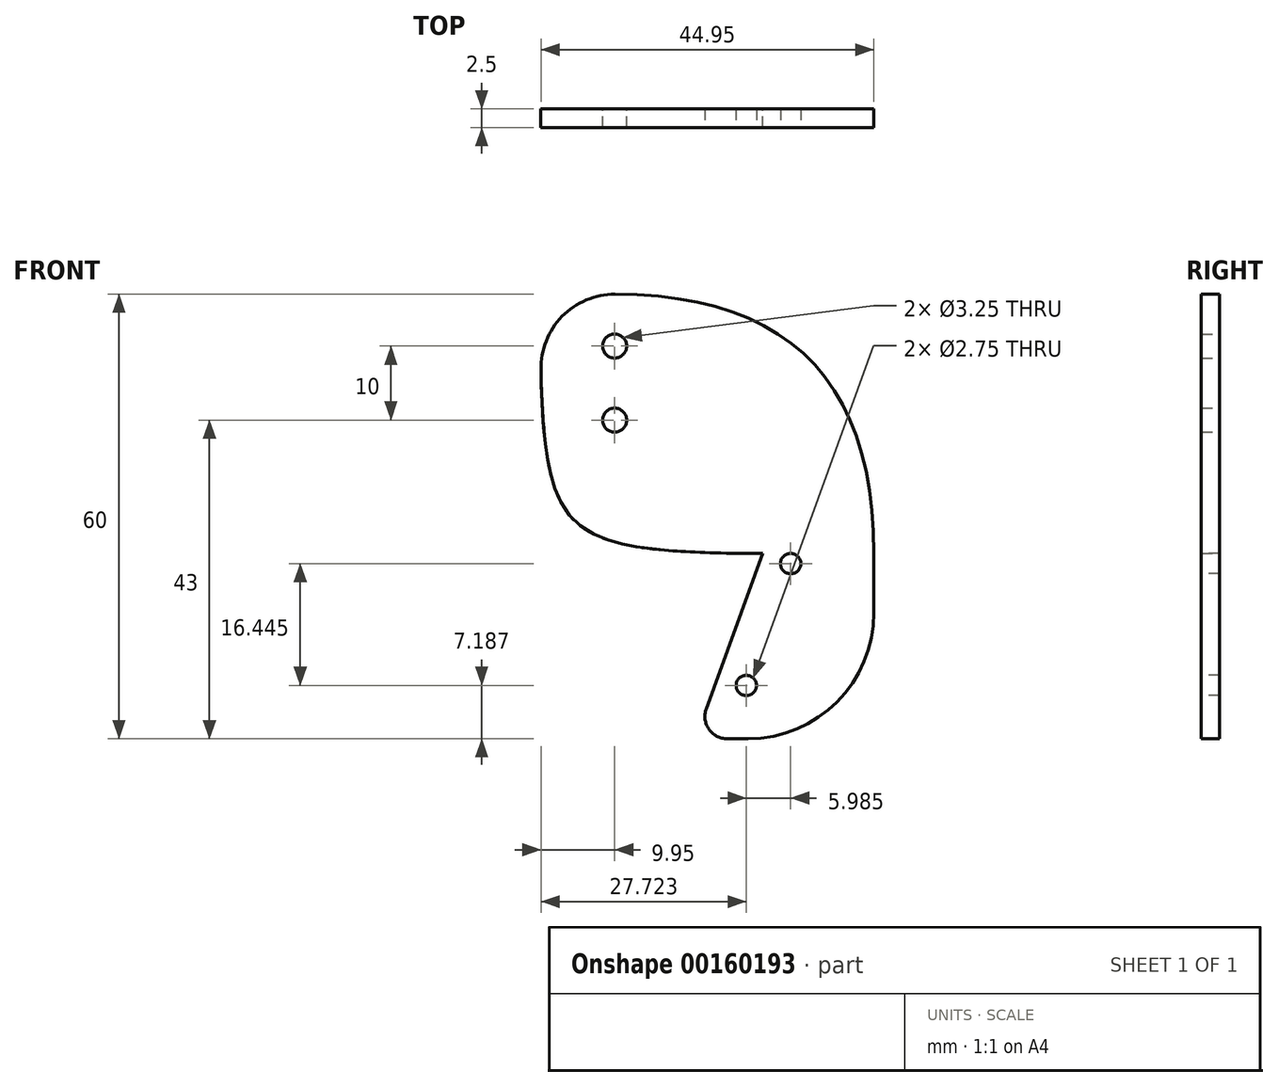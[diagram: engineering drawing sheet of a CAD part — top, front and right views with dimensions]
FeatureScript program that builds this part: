
annotation { "Feature Type Name" : "Feature", "Feature Type Description" : "" }
export const myFeature = defineFeature(function(context is Context, id is Id, definition is map)
    precondition{}
    {
        {
            var Q0;
            Q0=qCreatedBy(makeId("Front.planeOp"),FACE);
            var sketch = newSketch(context, id + "F0", { "sketchPlane" : qUnion([Q0])});
            skLineSegment(sketch, "E0.left", {"start": v(-30, 35) * mm, "end": v(-30, 0) * mm});
            skPoint(sketch, "E0.middle", {"position": v(0, 0) * mm});
            skLineSegment(sketch, "E1", {"start": v(-9.1, 9.88) * mm, "end": v(-9.1, 9.88) * mm});
            skCircle(sketch, "E2", {"center": v(-20, 28) * mm, "radius": 1.63 * mm});
            skCircle(sketch, "E3", {"center": v(-20, 18) * mm, "radius": 1.63 * mm});
            skLineSegment(sketch, "E4", {"start": v(-30, 0) * mm, "end": v(0, 0) * mm});
            skLineSegment(sketch, "E5", {"start": v(0, 0) * mm, "end": v(-9.1, -25) * mm});
            skLineSegment(sketch, "E6", {"start": v(-30, 35) * mm, "end": v(15, 35) * mm});
            skLineSegment(sketch, "E7", {"start": v(15, 35) * mm, "end": v(15, -25) * mm});
            skLineSegment(sketch, "E8", {"start": v(15, -25) * mm, "end": v(-9.1, -25) * mm});
            skSolve(sketch);
        }
        {
            var Q0;
            Q0 = qSketchRegion(id + "F0", true);
            extrude(context, id + "F1", {"entities" : qUnion([Q0]), "depth" : 2.5 * mm});
        }
        {
            var Q0;
            Q0=makeQuery(id+"F1.opExtrude","CAP_FACE",FACE,{"disambiguationData":[OSD([sQuery(id+"F0.wireOp",EDGE,"E0.bottom"),sQuery(id+"F0.wireOp",EDGE,"E0.top"),sQuery(id+"F0.wireOp",EDGE,"E0.left"),sQuery(id+"F0.wireOp",EDGE,"E2"),sQuery(id+"F0.wireOp",EDGE,"E3"),sQuery(id+"F0.wireOp",EDGE,"E4"),sQuery(id+"F0.wireOp",EDGE,"E5"),sQuery(id+"F0.wireOp",EDGE,"5cec1b2e-8655-48e0-9f0e-3a1df0f45c1c.filletArc"),sQuery(id+"F0.wireOp",EDGE,"c3276cd1-25e8-4f74-9dd4-febdcac5cc33.filletArc"),sQuery(id+"F0.wireOp",EDGE,"264a5dfb-2fea-4390-acd9-26117eb1927d.filletArc"),sQuery(id+"F0.wireOp",EDGE,"e464f4b8-703c-4172-9f04-898555628204.filletArc")])],"isStart":false});
            var sketch = newSketch(context, id + "F2", { "sketchPlane" : qUnion([Q0])});
            skCircle(sketch, "E9", {"center": v(3.76, -1.37) * mm, "radius": 1.38 * mm});
            skCircle(sketch, "E10", {"center": v(-2.23, -17.81) * mm, "radius": 1.38 * mm});
            skLineSegment(sketch, "E11", {"start": v(3.76, -1.37) * mm, "end": v(0, 0) * mm, "construction": true});
            skSolve(sketch);
        }
        {
            var Q0;
            Q0 = qSketchRegion(id + "F2", true);
            extrude(context, id + "F3", {"entities" : qUnion([Q0]), "operationType" : NewBodyOperationType.REMOVE, "endBound" : BoundingType.THROUGH_ALL, "oppositeDirection" : true, "depth" : 25 * mm});
        }
        {
            var Q0;
            Q0=makeQuery(id+"F1.opExtrude","SWEPT_EDGE",EDGE,{"disambiguationData":[OSD([sQuery(id+"F0.wireOp",EDGE,"E6"),sQuery(id+"F0.wireOp",EDGE,"E7")])]});
            fillet(context, id + "F4", {"entities" : qUnion([Q0]), "radius" : 35 * mm, "tangentPropagation" : true, "rho" : .5, "crossSection" : FilletCrossSection.CONIC, "allowEdgeOverflow" : false});
        }
        {
            var Q0;
            Q0=makeQuery(id+"F1.opExtrude","SWEPT_EDGE",EDGE,{"disambiguationData":[OSD([sQuery(id+"F0.wireOp",EDGE,"E7"),sQuery(id+"F0.wireOp",EDGE,"E8")])]});
            fillet(context, id + "F5", {"entities" : qUnion([Q0]), "radius" : 17 * mm, "tangentPropagation" : true, "allowEdgeOverflow" : false});
        }
        {
            var Q0;
            Q0=makeQuery(id+"F4.opFillet","BLEND_EDGE",EDGE,{"blendedFrom":[makeQuery(id+"F1.opExtrude","SWEPT_EDGE",EDGE,{"disambiguationData":[OSD([sQuery(id+"F0.wireOp",EDGE,"E6"),sQuery(id+"F0.wireOp",EDGE,"E7")])]}),makeQuery(id+"F1.opExtrude","SWEPT_FACE",FACE,{"disambiguationData":[OSD([sQuery(id+"F0.wireOp",EDGE,"E0.left")])]})],"blendedInto":[makeQuery(id+"F1.opExtrude","SWEPT_FACE",FACE,{"disambiguationData":[OSD([sQuery(id+"F0.wireOp",EDGE,"E0.left")])]})]});
            var Q1;
            Q1=makeQuery(id+"F1.opExtrude","SWEPT_EDGE",EDGE,{"disambiguationData":[OSD([sQuery(id+"F0.wireOp",EDGE,"E0.left"),sQuery(id+"F0.wireOp",EDGE,"E4")])]});
            fillet(context, id + "F6", {"entities" : qUnion([Q0, Q1]), "radius" : 30 * mm, "tangentPropagation" : true, "rho" : .7, "crossSection" : FilletCrossSection.CONIC, "allowEdgeOverflow" : false});
        }
        {
            var Q0;
            Q0=makeQuery(id+"F1.opExtrude","SWEPT_EDGE",EDGE,{"disambiguationData":[OSD([sQuery(id+"F0.wireOp",EDGE,"E5"),sQuery(id+"F0.wireOp",EDGE,"E8")])]});
            fillet(context, id + "F7", {"entities" : qUnion([Q0]), "radius" : 3 * mm, "tangentPropagation" : true, "allowEdgeOverflow" : false});
        }
        {
            var Q0;
            Q0=makeQuery(id+"F1.opExtrude","SWEPT_EDGE",EDGE,{"disambiguationData":[OSD([sQuery(id+"F0.wireOp",EDGE,"E0.left"),sQuery(id+"F0.wireOp",EDGE,"E6")])]});
            fillet(context, id + "F8", {"entities" : qUnion([Q0]), "radius" : 10 * mm, "tangentPropagation" : true, "allowEdgeOverflow" : false});
        }
    });
